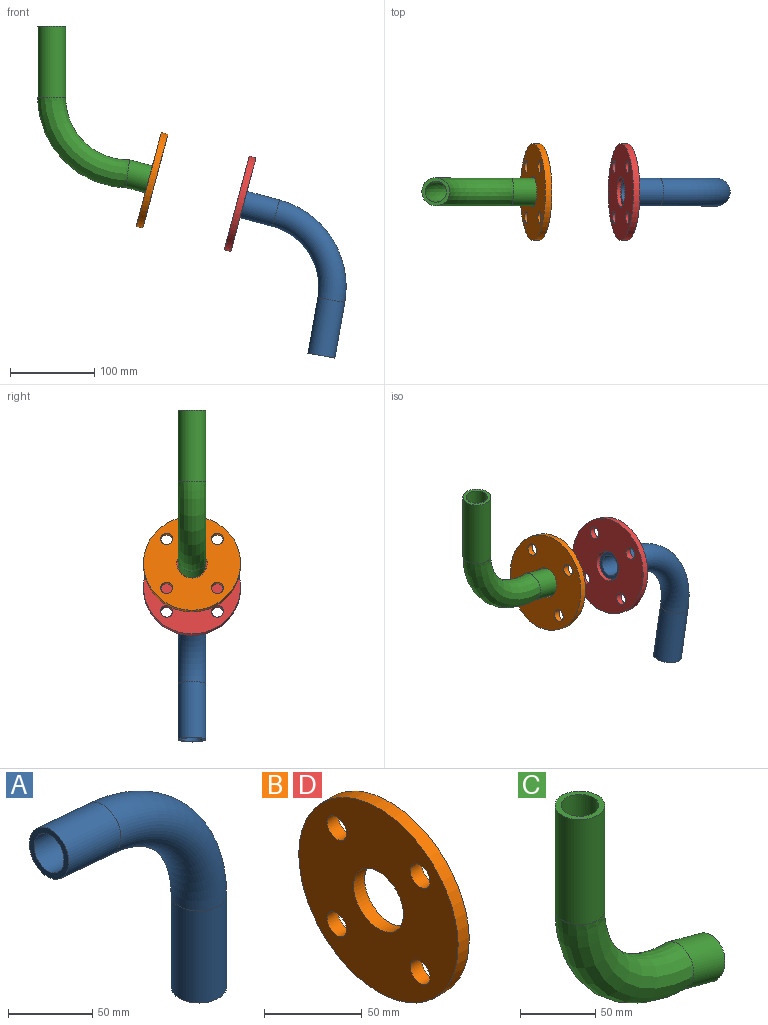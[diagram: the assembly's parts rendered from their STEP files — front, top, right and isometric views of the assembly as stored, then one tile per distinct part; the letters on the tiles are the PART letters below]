
ASSEMBLY  parts=4 mates=3
PART A: 8 faces, bbox 152.7x33x181.8 mm
  f0: cylinder r=12.5mm len=67mm, axis (0,0,1), area 5262.2mm2, adj f1,f2
  f1: torus R=90mm, axis (0,-1,0), area 10486.5mm2, adj f0,f5
  f2: plane 33x33mm, normal (0,0,-1), area 364.4mm2, adj f0,f3
  f3: cylinder r=16.5mm len=67mm, axis (0,0,1), area 6946.1mm2, adj f2,f4
  f4: torus R=90mm, axis (0,-1,0), area 13842.1mm2, adj f3,f6
  f5: cylinder r=12.5mm len=46.01mm, axis (1,0,-0.09), area 3455.8mm2, adj f1,f7
  f6: cylinder r=16.5mm len=46.71mm, axis (1,0,-0.09), area 4561.6mm2, adj f4,f7
  f7: plane 33x32.87mm, normal (-1,0,0.09), area 364.4mm2, adj f5,f6
PART B: 8 faces, bbox 8x115x115 mm
  f0: cylinder r=18mm len=36mm, axis (-1,0,0), area 904.8mm2, adj f6,f7
  f1: cylinder r=7mm len=14mm, axis (-1,0,0), area 351.9mm2, adj f6,f7
  f2: cylinder r=7mm len=14mm, axis (-1,0,0), area 351.9mm2, adj f6,f7
  f3: cylinder r=7mm len=14mm, axis (-1,0,0), area 351.9mm2, adj f6,f7
  f4: cylinder r=7mm len=14mm, axis (-1,0,0), area 351.9mm2, adj f6,f7
  f5: cylinder r=57.5mm len=115mm, axis (-1,0,0), area 2890.3mm2, adj f6,f7
  f6: plane 115x115mm, normal (1,0,0), area 8753.3mm2, adj f0,f1,f2,f3,f4,f5
  f7: plane 115x115mm, normal (-1,0,0), area 8753.3mm2, adj f0,f1,f2,f3,f4,f5
PART C: 8 faces, bbox 139.7x66x198.8 mm
  f0: cylinder r=12.5mm len=37.04mm, axis (0.97,0,-0.26), area 2357.3mm2, adj f2,f3
  f1: cylinder r=12.5mm len=85.1mm, axis (0,0,-1), area 6683.7mm2, adj f2,f4
  f2: bspline ~104.41x102.5mm, area 11098.4mm2, adj f0,f1
  f3: plane 33x31.88mm, normal (0.97,0,-0.26), area 364.4mm2, adj f0,f5
  f4: plane 33x33mm, normal (0,0,1), area 364.4mm2, adj f1,f6
  f5: cylinder r=16.5mm len=40.2mm, axis (0.97,0,-0.26), area 3112.6mm2, adj f3,f7
  f6: cylinder r=16.5mm len=85.1mm, axis (0,0,-1), area 8822.5mm2, adj f4,f7
  f7: bspline ~108.99x106.5mm, area 14648.8mm2, adj f5,f6
PART D: same geometry as B
PLACE A rot(axis=(0,1,0),10deg) t=(256.99,-71.69,-389.24)mm
PLACE B rot(axis=(0,1,0),15deg) t=(52.61,-71.69,-180.32)mm
PLACE C t=(-62.51,-71.69,1.51)mm fixed
PLACE D rot(axis=(0,1,0),15deg) t=(156.93,-71.69,-208.27)mm
MATE fastened B.f0 <-> C.f5  axis (-0.97,0,0.26) through (56.47,-71.69,-181.36)mm
MATE fastened B.f1 <-> D.f1  axis (0.97,0,-0.26) through (68.11,-101.74,-153.36)mm
MATE fastened D.f5 <-> A.f5  axis (0.97,0,-0.26) through (164.65,-71.69,-210.34)mm
